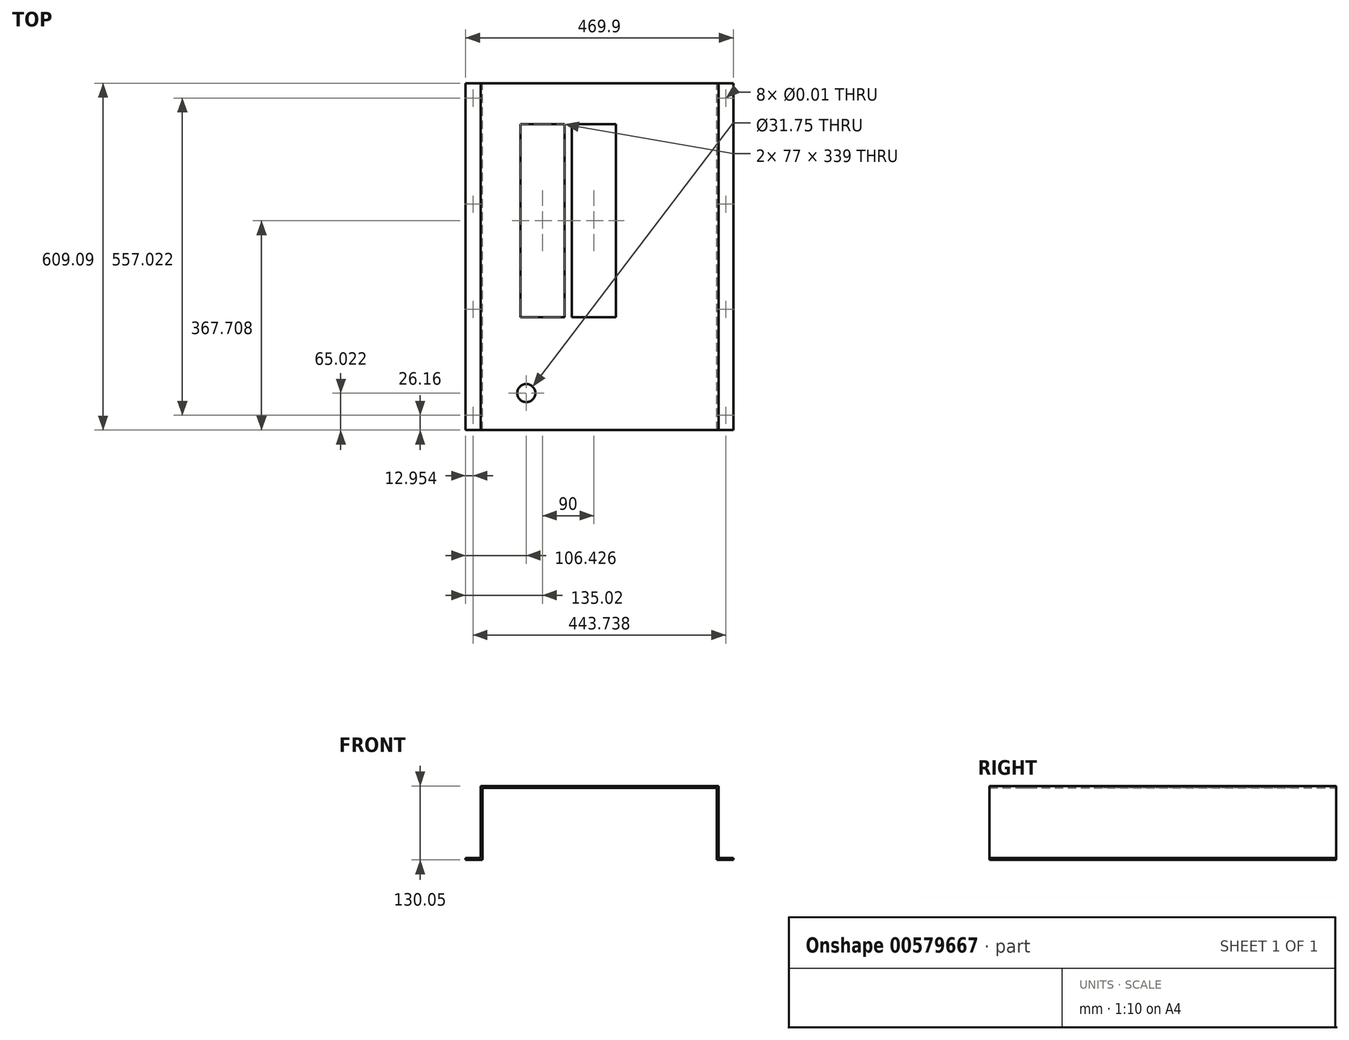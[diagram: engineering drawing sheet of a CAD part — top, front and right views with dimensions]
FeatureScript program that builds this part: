
annotation { "Feature Type Name" : "Feature", "Feature Type Description" : "" }
export const myFeature = defineFeature(function(context is Context, id is Id, definition is map)
    precondition{}
    {
        {
            var Q0;
            Q0=qCreatedBy(makeId("Front.planeOp"),FACE);
            var sketch = newSketch(context, id + "F0", { "sketchPlane" : qUnion([Q0])});
            skLineSegment(sketch, "E0", {"start": v(0, 0) * mm, "end": v(-25.9, 0) * mm});
            skLineSegment(sketch, "E1", {"start": v(-25.9, 0) * mm, "end": v(-25.9, 126.87) * mm});
            skLineSegment(sketch, "E2", {"start": v(-25.9, 126.87) * mm, "end": v(-443.74, 126.87) * mm});
            skLineSegment(sketch, "E3", {"start": v(-443.74, 126.87) * mm, "end": v(-443.74, 0) * mm});
            skLineSegment(sketch, "E4", {"start": v(-443.74, 0) * mm, "end": v(-469.9, 0) * mm});
            skLineSegment(sketch, "E5", {"start": v(-469.9, 0) * mm, "end": v(-469.9, -3.18) * mm});
            skLineSegment(sketch, "E6", {"start": v(-469.9, -3.18) * mm, "end": v(-440.56, -3.18) * mm});
            skLineSegment(sketch, "E7", {"start": v(-440.56, -3.18) * mm, "end": v(-440.56, 123.7) * mm});
            skLineSegment(sketch, "E8", {"start": v(-440.56, 123.7) * mm, "end": v(-29.08, 123.7) * mm});
            skLineSegment(sketch, "E9", {"start": v(-29.08, 123.7) * mm, "end": v(-29.08, -3.18) * mm});
            skLineSegment(sketch, "E10", {"start": v(-29.08, -3.18) * mm, "end": v(0, -3.18) * mm});
            skLineSegment(sketch, "E11", {"start": v(0, -3.18) * mm, "end": v(0, 0) * mm});
            skSolve(sketch);
        }
        {
            var Q0;
            Q0=makeQuery(id+"F0.imprint","IMPRINT",FACE,{"disambiguationData":[TD([[makeQuery(id+"F0.imprint","IMPRINT",EDGE,{"derivedFrom":sQuery(id+"F0.wireOp",EDGE,"E0")}),1.0]])]});
            extrude(context, id + "F1", {"entities" : qUnion([Q0]), "depth" : 609.1 * mm, "offsetDistance" : 25.4 * mm});
        }
        {
            var Q0;
            Q0=makeQuery(id+"F1.opExtrude","SWEPT_FACE",FACE,{"disambiguationData":[OSD([sQuery(id+"F0.wireOp",EDGE,"E2")])]});
            var sketch = newSketch(context, id + "F2", { "sketchPlane" : qUnion([Q0])});
            skLineSegment(sketch, "E12.bottom", {"start": v(-373.38, -71.88) * mm, "end": v(-296.38, -71.88) * mm});
            skLineSegment(sketch, "E12.top", {"start": v(-373.38, -410.88) * mm, "end": v(-296.38, -410.88) * mm});
            skLineSegment(sketch, "E12.left", {"start": v(-373.38, -71.88) * mm, "end": v(-373.38, -410.88) * mm});
            skLineSegment(sketch, "E12.right", {"start": v(-296.38, -71.88) * mm, "end": v(-296.38, -410.88) * mm});
            skLineSegment(sketch, "E13.bottom", {"start": v(-283.38, -71.88) * mm, "end": v(-206.38, -71.88) * mm});
            skLineSegment(sketch, "E13.top", {"start": v(-283.38, -410.88) * mm, "end": v(-206.38, -410.88) * mm});
            skLineSegment(sketch, "E13.left", {"start": v(-283.38, -71.88) * mm, "end": v(-283.38, -410.88) * mm});
            skLineSegment(sketch, "E13.right", {"start": v(-206.38, -71.88) * mm, "end": v(-206.38, -410.88) * mm});
            skSolve(sketch);
        }
        {
            var Q0;
            Q0 = qSketchRegion(id + "F2", true);
            extrude(context, id + "F3", {"entities" : qUnion([Q0]), "operationType" : NewBodyOperationType.REMOVE, "oppositeDirection" : true, "depth" : 25.4 * mm, "offsetDistance" : 25.4 * mm});
        }
        {
            var Q0;
            Q0=makeQuery(id+"F1.opExtrude","SWEPT_FACE",FACE,{"disambiguationData":[OSD([sQuery(id+"F0.wireOp",EDGE,"E2")])]});
            var sketch = newSketch(context, id + "F4", { "sketchPlane" : qUnion([Q0])});
            skCircle(sketch, "E14", {"center": v(-363.47, -544.07) * mm, "radius": 15.88 * mm});
            skSolve(sketch);
        }
        {
            var Q0;
            Q0 = qSketchRegion(id + "F4", true);
            extrude(context, id + "F5", {"entities" : qUnion([Q0]), "operationType" : NewBodyOperationType.REMOVE, "oppositeDirection" : true, "depth" : 25.4 * mm, "offsetDistance" : 25.4 * mm});
        }
        {
            var Q0;
            Q0=makeQuery(id+"F1.opExtrude","SWEPT_FACE",FACE,{"disambiguationData":[OSD([sQuery(id+"F0.wireOp",EDGE,"E0")])]});
            var sketch = newSketch(context, id + "F6", { "sketchPlane" : qUnion([Q0])});
            skPoint(sketch, "E15", {"position": v(-456.95, -25.9) * mm});
            skPoint(sketch, "E16", {"position": v(-456.95, -212.1) * mm});
            skPoint(sketch, "E17", {"position": v(-456.95, -397) * mm});
            skPoint(sketch, "E18", {"position": v(-456.95, -582.93) * mm});
            skPoint(sketch, "E19", {"position": v(-13.2, -582.93) * mm});
            skPoint(sketch, "E20", {"position": v(-13.2, -397) * mm});
            skPoint(sketch, "E21", {"position": v(-13.2, -212.1) * mm});
            skPoint(sketch, "E22", {"position": v(-13.2, -25.9) * mm});
            skSolve(sketch);
        }
        {
            var Q0;
            Q0=sQuery(id+"F6.wireOp",VERTEX,"E15");
            var Q1;
            Q1=sQuery(id+"F6.wireOp",VERTEX,"E16");
            var Q2;
            Q2=sQuery(id+"F6.wireOp",VERTEX,"E17");
            var Q3;
            Q3=sQuery(id+"F6.wireOp",VERTEX,"E18");
            var Q4;
            Q4=sQuery(id+"F6.wireOp",VERTEX,"E19");
            var Q5;
            Q5=sQuery(id+"F6.wireOp",VERTEX,"E20");
            var Q6;
            Q6=sQuery(id+"F6.wireOp",VERTEX,"E21");
            var Q7;
            Q7=sQuery(id+"F6.wireOp",VERTEX,"E22");
            var Q8;
            Q8=makeQuery(id+"F1.opExtrude","SWEPT_BODY",BODY,{"disambiguationData":[OSD([sQuery(id+"F0.wireOp",EDGE,"E0"),sQuery(id+"F0.wireOp",EDGE,"E1"),sQuery(id+"F0.wireOp",EDGE,"E2"),sQuery(id+"F0.wireOp",EDGE,"E3"),sQuery(id+"F0.wireOp",EDGE,"E4"),sQuery(id+"F0.wireOp",EDGE,"E5"),sQuery(id+"F0.wireOp",EDGE,"E6"),sQuery(id+"F0.wireOp",EDGE,"E7"),sQuery(id+"F0.wireOp",EDGE,"E8"),sQuery(id+"F0.wireOp",EDGE,"E9"),sQuery(id+"F0.wireOp",EDGE,"E10"),sQuery(id+"F0.wireOp",EDGE,"E11")])]});
            hole(context, id + "F7", {"style" : HoleStyle.SIMPLE, "endStyle" : HoleEndStyle.THROUGH, "standardTappedOrClearance" : lookupTablePath({ "standard" : "ANSI", "size" : "9/32 (0.28)", "type" : "Drilled" }), "standardBlindInLast" : lookupTablePath({ "standard" : "ANSI", "size" : "9/32", "type" : "Drilled" }), "holeDiameter" : 9 / 812.8 * mm, "isTappedThrough" : true, "tappedDepth" : 8.9 * mm, "tapClearance" : 1, "locations" : qUnion([Q0, Q1, Q2, Q3, Q4, Q5, Q6, Q7]), "scope" : qUnion([Q8])});
        }
    });
